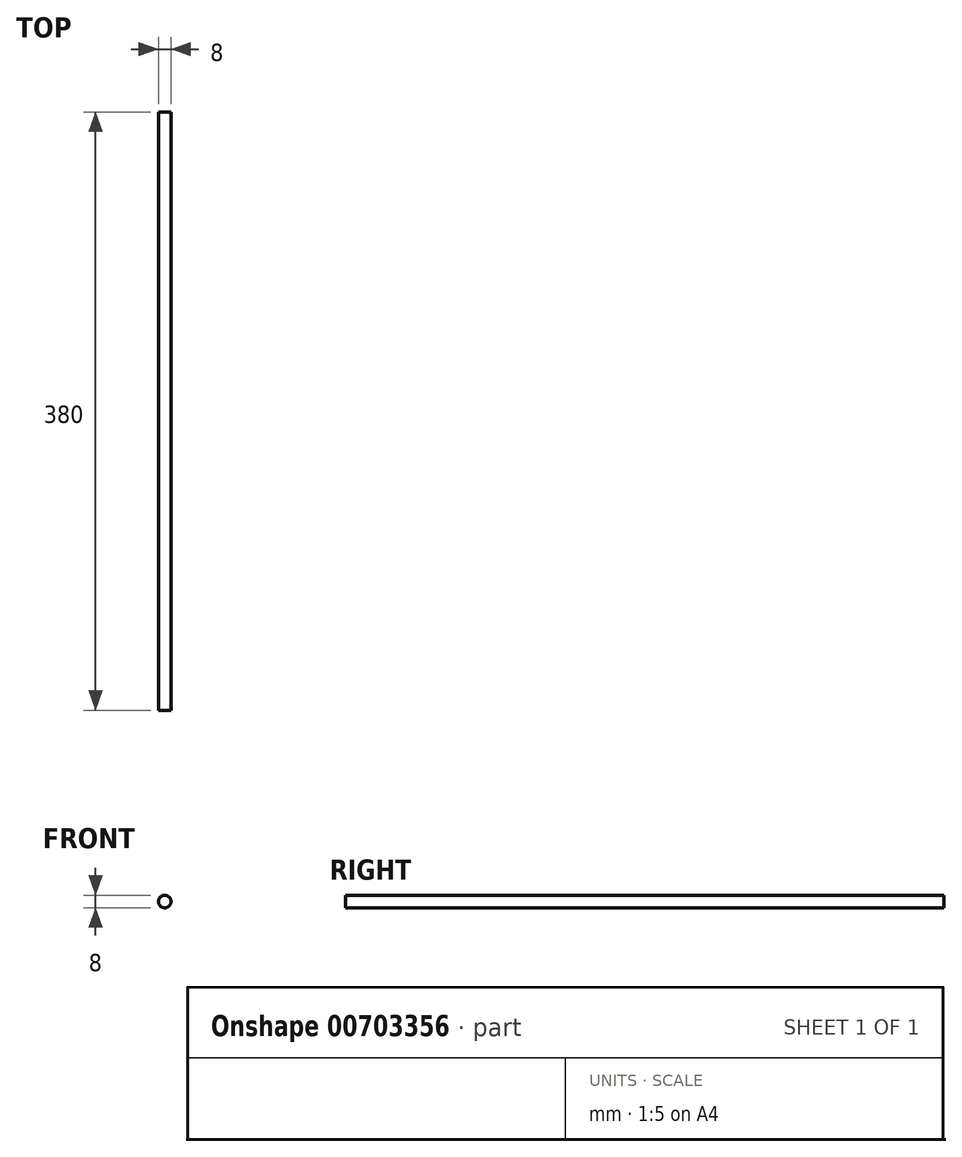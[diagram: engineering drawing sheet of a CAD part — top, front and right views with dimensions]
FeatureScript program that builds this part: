
annotation { "Feature Type Name" : "Feature", "Feature Type Description" : "" }
export const myFeature = defineFeature(function(context is Context, id is Id, definition is map)
    precondition{}
    {
        {
            var Q0;
            Q0=qCreatedBy(makeId("Front.planeOp"),FACE);
            var sketch = newSketch(context, id + "F0", { "sketchPlane" : qUnion([Q0])});
            skCircle(sketch, "E0", {"center": v(0, 0) * mm, "radius": 4 * mm});
            skSolve(sketch);
        }
        {
            var Q0;
            Q0 = qSketchRegion(id + "F0", true);
            extrude(context, id + "F1", {"entities" : qUnion([Q0]), "oppositeDirection" : true, "depth" : 380 * mm, "offsetDistance" : 25 * mm});
        }
    });
